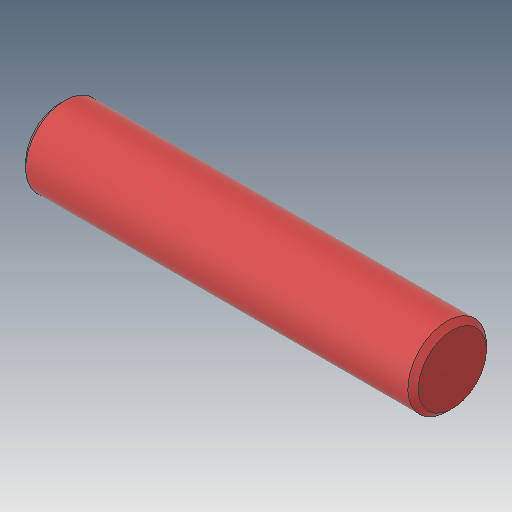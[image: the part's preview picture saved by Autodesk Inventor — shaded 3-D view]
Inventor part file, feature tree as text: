
AUTODESK INVENTOR PART (.ipt)
format: ipt  version: 2019.4 (Build 234330000, 330)  size: 102,400 bytes
history: native  units: mm
features: other x1, extrude x1, chamfer x1, sketch x1
ambient origin geometry x8: Origin, YZ Plane, XZ Plane, XY Plane, X Axis, Y Axis, Z Axis, Center Point
bodies: Body1 (feature_tree)
feature tree (4):
  other  "ソリッド1"
  extrude  "押し出し1"  Depth=3.0mm
  chamfer  "面取り1"  Distance=15.0mm
  sketch  "スケッチ1"
